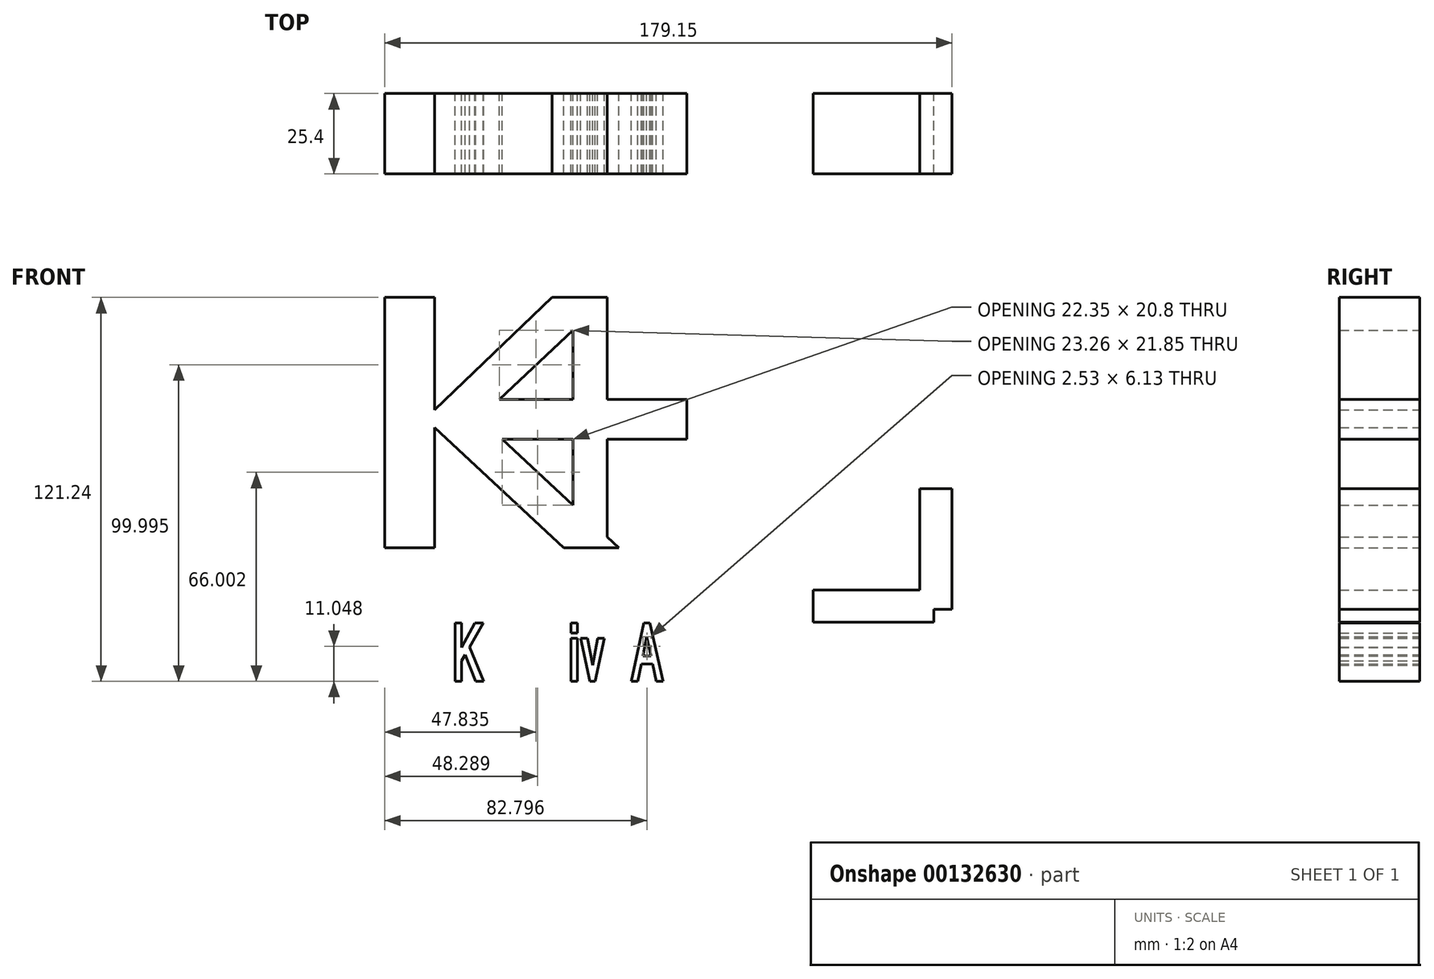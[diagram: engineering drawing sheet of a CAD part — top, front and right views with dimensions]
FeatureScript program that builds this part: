
annotation { "Feature Type Name" : "Feature", "Feature Type Description" : "" }
export const myFeature = defineFeature(function(context is Context, id is Id, definition is map)
    precondition{}
    {
        {
            var Q0;
            Q0=qCreatedBy(makeId("Front.planeOp"),FACE);
            var sketch = newSketch(context, id + "F0", { "sketchPlane" : qUnion([Q0])});
            skLineSegment(sketch, "E0", {"start": v(-20.88, -11.83) * mm, "end": v(-20.88, 8.97) * mm});
            skLineSegment(sketch, "E1", {"start": v(-20.88, 8.97) * mm, "end": v(-43.23, 8.97) * mm});
            skLineSegment(sketch, "E2", {"start": v(-43.23, 8.97) * mm, "end": v(-20.88, -11.83) * mm});
            skLineSegment(sketch, "E3", {"start": v(-20.88, 43.5) * mm, "end": v(-44.13, 21.64) * mm});
            skLineSegment(sketch, "E4", {"start": v(-44.13, 21.64) * mm, "end": v(-20.88, 21.64) * mm});
            skLineSegment(sketch, "E5", {"start": v(-20.88, 21.64) * mm, "end": v(-20.88, 43.5) * mm});
            skLineSegment(sketch, "E6", {"start": v(3.72, -59.45) * mm, "end": v(2.43, -53.32) * mm});
            skLineSegment(sketch, "E7", {"start": v(2.43, -53.32) * mm, "end": v(1.2, -59.45) * mm});
            skLineSegment(sketch, "E8", {"start": v(1.2, -59.45) * mm, "end": v(3.72, -59.45) * mm});
            skLineSegment(sketch, "E9", {"start": v(-64.6, 53.8) * mm, "end": v(-80.34, 53.8) * mm});
            skLineSegment(sketch, "E10", {"start": v(-80.34, 53.8) * mm, "end": v(-80.34, -25.29) * mm});
            skLineSegment(sketch, "E11", {"start": v(-80.34, -25.29) * mm, "end": v(-64.6, -25.29) * mm});
            skLineSegment(sketch, "E12", {"start": v(-64.6, -25.29) * mm, "end": v(-64.6, 12.72) * mm});
            skLineSegment(sketch, "E13", {"start": v(-64.6, 12.72) * mm, "end": v(-23.74, -25.29) * mm});
            skLineSegment(sketch, "E14", {"start": v(-23.74, -25.29) * mm, "end": v(-6.42, -25.29) * mm});
            skLineSegment(sketch, "E15", {"start": v(-6.42, -25.29) * mm, "end": v(-10.13, -21.83) * mm});
            skLineSegment(sketch, "E16", {"start": v(-10.13, -21.83) * mm, "end": v(-10.13, 8.97) * mm});
            skLineSegment(sketch, "E17", {"start": v(-10.13, 8.97) * mm, "end": v(15.04, 8.97) * mm});
            skLineSegment(sketch, "E18", {"start": v(15.04, 8.97) * mm, "end": v(15.04, 21.64) * mm});
            skLineSegment(sketch, "E19", {"start": v(15.04, 21.64) * mm, "end": v(-10.13, 21.64) * mm});
            skLineSegment(sketch, "E20", {"start": v(-10.13, 21.64) * mm, "end": v(-10.13, 52.54) * mm});
            skLineSegment(sketch, "E21", {"start": v(-10.13, 52.54) * mm, "end": v(-10.13, 53.8) * mm});
            skLineSegment(sketch, "E22", {"start": v(-10.13, 53.8) * mm, "end": v(-10.38, 53.8) * mm});
            skLineSegment(sketch, "E23", {"start": v(-10.38, 53.8) * mm, "end": v(-27.47, 53.8) * mm});
            skLineSegment(sketch, "E24", {"start": v(-27.47, 53.8) * mm, "end": v(-64.6, 18.28) * mm});
            skLineSegment(sketch, "E25", {"start": v(-64.6, 18.28) * mm, "end": v(-64.6, 53.8) * mm});
            skLineSegment(sketch, "E26", {"start": v(-20.88, -11.83) * mm, "end": v(-43.23, 8.97) * mm});
            skLineSegment(sketch, "E27", {"start": v(-43.23, 8.97) * mm, "end": v(-20.88, 8.97) * mm});
            skLineSegment(sketch, "E28", {"start": v(-20.88, 8.97) * mm, "end": v(-20.88, -11.83) * mm});
            skLineSegment(sketch, "E29", {"start": v(-20.88, 43.5) * mm, "end": v(-20.88, 21.64) * mm});
            skLineSegment(sketch, "E30", {"start": v(-20.88, 21.64) * mm, "end": v(-44.13, 21.64) * mm});
            skLineSegment(sketch, "E31", {"start": v(-44.13, 21.64) * mm, "end": v(-20.88, 43.5) * mm});
            skLineSegment(sketch, "E32", {"start": v(-21.45, -48.96) * mm, "end": v(-21.45, -52.14) * mm});
            skLineSegment(sketch, "E33", {"start": v(-21.45, -52.14) * mm, "end": v(-19.48, -52.14) * mm});
            skLineSegment(sketch, "E34", {"start": v(-19.48, -52.14) * mm, "end": v(-19.48, -48.96) * mm});
            skLineSegment(sketch, "E35", {"start": v(-19.48, -48.96) * mm, "end": v(-19.84, -48.96) * mm});
            skLineSegment(sketch, "E36", {"start": v(-19.84, -48.96) * mm, "end": v(-21.45, -48.96) * mm});
            skLineSegment(sketch, "E37", {"start": v(-21.45, -53.87) * mm, "end": v(-21.45, -67.43) * mm});
            skLineSegment(sketch, "E38", {"start": v(-21.45, -67.43) * mm, "end": v(-19.48, -67.43) * mm});
            skLineSegment(sketch, "E39", {"start": v(-19.48, -67.43) * mm, "end": v(-19.48, -53.87) * mm});
            skLineSegment(sketch, "E40", {"start": v(-19.48, -53.87) * mm, "end": v(-19.84, -53.87) * mm});
            skLineSegment(sketch, "E41", {"start": v(-19.84, -53.87) * mm, "end": v(-21.45, -53.87) * mm});
            skLineSegment(sketch, "E42", {"start": v(-13.14, -54.15) * mm, "end": v(-14.68, -62.36) * mm});
            skLineSegment(sketch, "E43", {"start": v(-14.68, -62.36) * mm, "end": v(-16.28, -53.87) * mm});
            skLineSegment(sketch, "E44", {"start": v(-16.28, -53.87) * mm, "end": v(-18.39, -53.87) * mm});
            skLineSegment(sketch, "E45", {"start": v(-18.39, -53.87) * mm, "end": v(-15.54, -67.43) * mm});
            skLineSegment(sketch, "E46", {"start": v(-15.54, -67.43) * mm, "end": v(-13.83, -67.43) * mm});
            skLineSegment(sketch, "E47", {"start": v(-13.83, -67.43) * mm, "end": v(-11, -53.87) * mm});
            skLineSegment(sketch, "E48", {"start": v(-11, -53.87) * mm, "end": v(-13.08, -53.87) * mm});
            skLineSegment(sketch, "E49", {"start": v(-13.08, -53.87) * mm, "end": v(-13.14, -54.15) * mm});
            skLineSegment(sketch, "E50", {"start": v(3.14, -48.96) * mm, "end": v(1.44, -48.96) * mm});
            skLineSegment(sketch, "E51", {"start": v(1.44, -48.96) * mm, "end": v(-2.5, -67.43) * mm});
            skLineSegment(sketch, "E52", {"start": v(-2.5, -67.43) * mm, "end": v(-0.4, -67.43) * mm});
            skLineSegment(sketch, "E53", {"start": v(-0.4, -67.43) * mm, "end": v(0.7, -62.03) * mm});
            skLineSegment(sketch, "E54", {"start": v(0.7, -62.03) * mm, "end": v(4.25, -62.03) * mm});
            skLineSegment(sketch, "E55", {"start": v(4.25, -62.03) * mm, "end": v(5.39, -67.43) * mm});
            skLineSegment(sketch, "E56", {"start": v(5.39, -67.43) * mm, "end": v(7.6, -67.43) * mm});
            skLineSegment(sketch, "E57", {"start": v(7.6, -67.43) * mm, "end": v(3.42, -48.96) * mm});
            skLineSegment(sketch, "E58", {"start": v(3.42, -48.96) * mm, "end": v(3.14, -48.96) * mm});
            skLineSegment(sketch, "E59", {"start": v(3.72, -59.45) * mm, "end": v(1.2, -59.45) * mm});
            skLineSegment(sketch, "E60", {"start": v(1.2, -59.45) * mm, "end": v(2.43, -53.32) * mm});
            skLineSegment(sketch, "E61", {"start": v(2.43, -53.32) * mm, "end": v(3.72, -59.45) * mm});
            skLineSegment(sketch, "E62", {"start": v(-49.23, -48.96) * mm, "end": v(-51.8, -48.96) * mm});
            skLineSegment(sketch, "E63", {"start": v(-51.8, -48.96) * mm, "end": v(-56.05, -56.73) * mm});
            skLineSegment(sketch, "E64", {"start": v(-56.05, -56.73) * mm, "end": v(-56.05, -48.96) * mm});
            skLineSegment(sketch, "E65", {"start": v(-56.05, -48.96) * mm, "end": v(-58.06, -48.96) * mm});
            skLineSegment(sketch, "E66", {"start": v(-58.06, -48.96) * mm, "end": v(-58.06, -67.43) * mm});
            skLineSegment(sketch, "E67", {"start": v(-58.06, -67.43) * mm, "end": v(-56.05, -67.43) * mm});
            skLineSegment(sketch, "E68", {"start": v(-56.05, -67.43) * mm, "end": v(-56.05, -61) * mm});
            skLineSegment(sketch, "E69", {"start": v(-56.05, -61) * mm, "end": v(-54.93, -59.02) * mm});
            skLineSegment(sketch, "E70", {"start": v(-54.93, -59.02) * mm, "end": v(-51.6, -67.43) * mm});
            skLineSegment(sketch, "E71", {"start": v(-51.6, -67.43) * mm, "end": v(-49.12, -67.43) * mm});
            skLineSegment(sketch, "E72", {"start": v(-49.12, -67.43) * mm, "end": v(-53.57, -56.6) * mm});
            skLineSegment(sketch, "E73", {"start": v(-53.57, -56.6) * mm, "end": v(-49.23, -48.96) * mm});
            skLineSegment(sketch, "E74", {"start": v(93.03, -38.56) * mm, "end": v(93.03, -48.72) * mm});
            skLineSegment(sketch, "E75", {"start": v(93.03, -48.72) * mm, "end": v(54.93, -48.72) * mm});
            skLineSegment(sketch, "E76", {"start": v(54.93, -48.72) * mm, "end": v(54.93, -38.56) * mm});
            skLineSegment(sketch, "E77", {"start": v(54.93, -38.56) * mm, "end": v(93.03, -38.56) * mm});
            skLineSegment(sketch, "E78", {"start": v(88.65, -6.67) * mm, "end": v(98.81, -6.67) * mm});
            skLineSegment(sketch, "E79", {"start": v(98.81, -6.67) * mm, "end": v(98.81, -44.77) * mm});
            skLineSegment(sketch, "E80", {"start": v(98.81, -44.77) * mm, "end": v(88.65, -44.77) * mm});
            skLineSegment(sketch, "E81", {"start": v(88.65, -44.77) * mm, "end": v(88.65, -6.67) * mm});
            skSolve(sketch);
        }
        {
            var Q0;
            Q0 = qSketchRegion(id + "F0", true);
            extrude(context, id + "F1", {"entities" : qUnion([Q0]), "depth" : 25.4 * mm});
        }
    });
